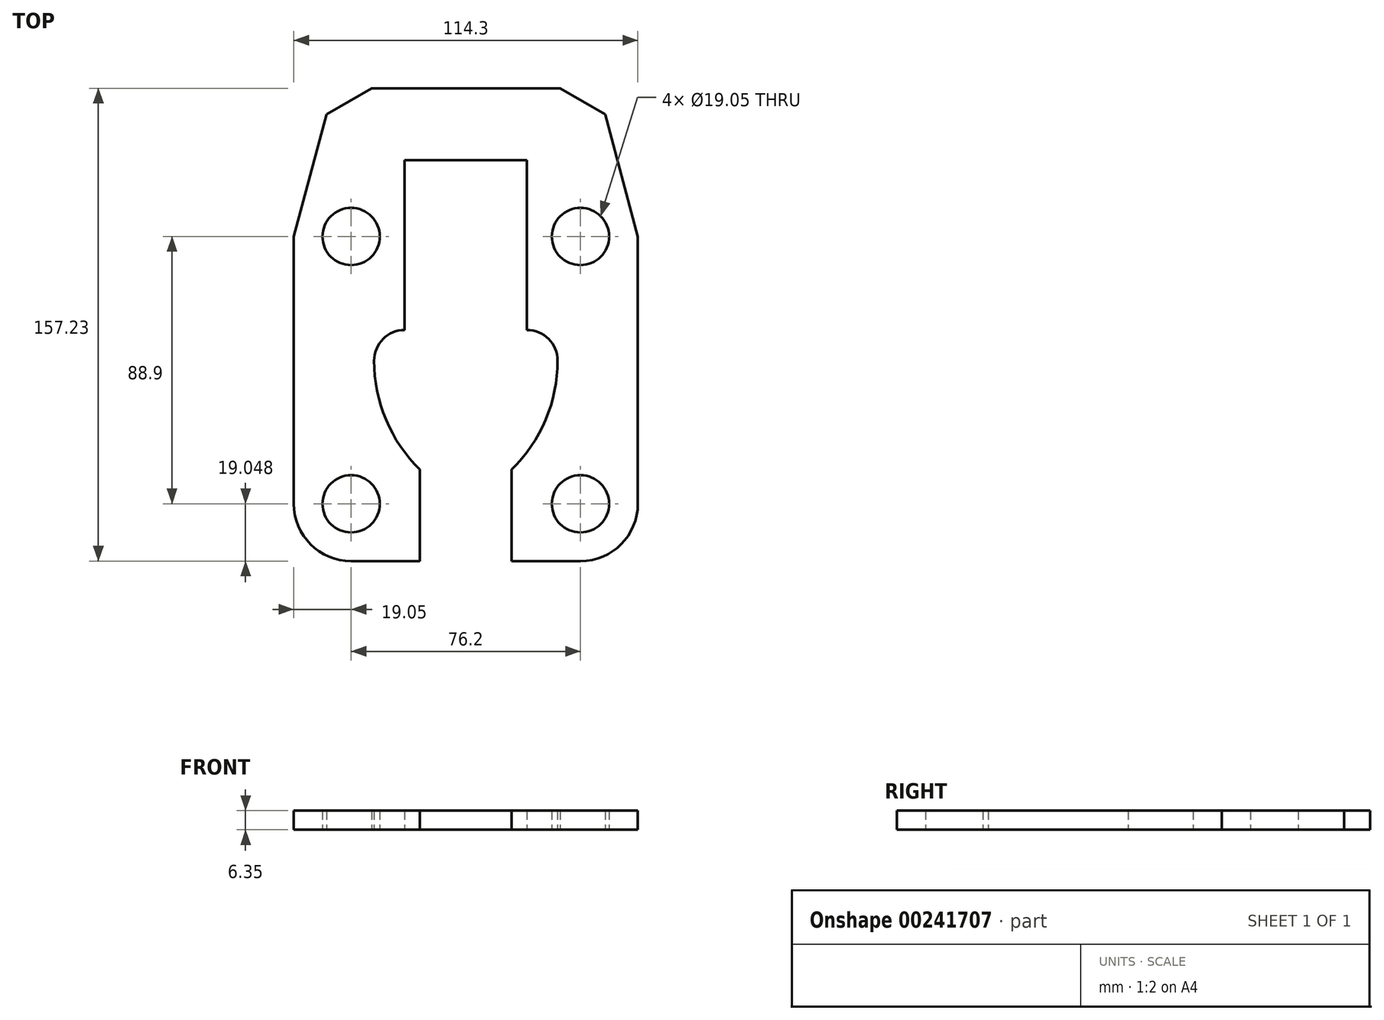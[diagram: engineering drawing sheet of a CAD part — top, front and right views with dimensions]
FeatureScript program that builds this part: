
annotation { "Feature Type Name" : "Feature", "Feature Type Description" : "" }
export const myFeature = defineFeature(function(context is Context, id is Id, definition is map)
    precondition{}
    {
        {
            var Q0;
            Q0=qCreatedBy(makeId("Top.planeOp"),FACE);
            var sketch = newSketch(context, id + "F0", { "sketchPlane" : qUnion([Q0])});
            skCircle(sketch, "E0", {"center": v(-38.1, -22.87) * mm, "radius": 9.53 * mm});
            skArc(sketch, "E1", {"start": v(-57.15, -22.87) * mm, "mid": v(-51.57, -36.34) * mm, "end": v(-38.1, -41.92) * mm});
            skLineSegment(sketch, "E2", {"start": v(-38.1, -41.92) * mm, "end": v(-15.24, -41.92) * mm});
            skLineSegment(sketch, "E3", {"start": v(-57.15, -22.87) * mm, "end": v(-57.15, 66.03) * mm});
            skCircle(sketch, "E4", {"center": v(-38.1, 66.03) * mm, "radius": 9.53 * mm});
            skLineSegment(sketch, "E5", {"start": v(-57.15, 66.03) * mm, "end": v(-46.26, 106.67) * mm});
            skLineSegment(sketch, "E6", {"start": v(-46.26, 106.67) * mm, "end": v(-31.3, 115.3) * mm});
            skLineSegment(sketch, "E7", {"start": v(-15.24, -41.92) * mm, "end": v(-15.24, -11.52) * mm});
            skLineSegment(sketch, "E8", {"start": v(-31.3, 115.3) * mm, "end": v(-15.24, 115.3) * mm});
            skLineSegment(sketch, "E9.bottom", {"start": v(-20.32, 91.43) * mm, "end": v(0, 91.43) * mm});
            skLineSegment(sketch, "E9.top", {"start": v(-15.24, 115.3) * mm, "end": v(0, 115.3) * mm});
            skArc(sketch, "E10", {"start": v(-20.32, 34.91) * mm, "mid": v(-27.5, 31.94) * mm, "end": v(-30.48, 24.75) * mm});
            skPoint(sketch, "E10.centerSnap0", {"position": v(-15.24, 24.75) * mm});
            skLineSegment(sketch, "E11", {"start": v(-20.32, 91.43) * mm, "end": v(-20.32, 34.91) * mm});
            skPoint(sketch, "E12", {"position": v(-15.24, 15.96) * mm});
            skPoint(sketch, "E13", {"position": v(-15.24, 33.55) * mm});
            skPoint(sketch, "E14.trimOffspring.end.orphan", {"position": v(-15.24, 91.43) * mm});
            skLineSegment(sketch, "E15.MirrorCS", {"start": v(20.32, 91.43) * mm, "end": v(0, 91.43) * mm});
            skPoint(sketch, "E16.MirrorP", {"position": v(15.24, 24.75) * mm});
            skLineSegment(sketch, "E17.MirrorCS", {"start": v(15.24, -41.92) * mm, "end": v(15.24, -11.52) * mm});
            skLineSegment(sketch, "E18.MirrorCS", {"start": v(38.1, -41.92) * mm, "end": v(15.24, -41.92) * mm});
            skLineSegment(sketch, "E19.MirrorCS", {"start": v(46.26, 106.67) * mm, "end": v(31.3, 115.3) * mm});
            skPoint(sketch, "E20.MirrorP", {"position": v(15.24, 91.43) * mm});
            skPoint(sketch, "E21.MirrorP", {"position": v(15.24, 33.55) * mm});
            skLineSegment(sketch, "E22.MirrorCS", {"start": v(57.15, -22.87) * mm, "end": v(57.15, 66.03) * mm});
            skLineSegment(sketch, "E23.MirrorCS", {"start": v(57.15, 66.03) * mm, "end": v(46.26, 106.67) * mm});
            skCircle(sketch, "E24.MirrorC", {"center": v(38.1, -22.87) * mm, "radius": 9.53 * mm});
            skLineSegment(sketch, "E25.MirrorCS", {"start": v(31.3, 115.3) * mm, "end": v(15.24, 115.3) * mm});
            skLineSegment(sketch, "E26.MirrorCS", {"start": v(15.24, 115.3) * mm, "end": v(0, 115.3) * mm});
            skLineSegment(sketch, "E27.MirrorCS", {"start": v(20.32, 91.43) * mm, "end": v(20.32, 24.75) * mm});
            skArc(sketch, "E28.MirrorCS", {"start": v(57.15, -22.87) * mm, "mid": v(51.57, -36.34) * mm, "end": v(38.1, -41.92) * mm});
            skArc(sketch, "E29.MirrorC", {"start": v(20.32, 34.91) * mm, "mid": v(27.5, 31.94) * mm, "end": v(30.48, 24.75) * mm});
            skPoint(sketch, "E30.MirrorP", {"position": v(15.24, 15.96) * mm});
            skCircle(sketch, "E31.MirrorC", {"center": v(38.1, 66.03) * mm, "radius": 9.53 * mm});
            skArc(sketch, "E32.trimOffspring", {"start": v(15.24, -11.52) * mm, "mid": v(26.52, 5.08) * mm, "end": v(30.48, 24.75) * mm});
            skArc(sketch, "E33", {"start": v(-30.48, 24.75) * mm, "mid": v(-26.52, 5.08) * mm, "end": v(-15.24, -11.52) * mm});
            skSolve(sketch);
        }
        {
            var Q0;
            Q0=makeQuery(id+"F0.imprint","IMPRINT",FACE,{"disambiguationData":[TD([[makeQuery(id+"F0.imprint","IMPRINT",EDGE,{"derivedFrom":sQuery(id+"F0.wireOp",EDGE,"E0")}),-1.0]])]});
            extrude(context, id + "F1", {"entities" : qUnion([Q0]), "depth" : 6.35 * mm});
        }
    });
